# Revit family: IS_ConnectAir_A7012_BIM_DE
name_source: partatom
category: Plumbing Fixtures
revit_build: Autodesk Revit MEP 2015 (Build: 20140606_1530(x64)
units: mm (PartAtom-declared; Revit-internal decimal feet)

## types (1)
- A7012AA - CONNCT AIR BSN MXR RMTD SLM GR PU/M
    BIMobject category = Taps & Mixers
    BOSUseNativeGeometries = 1
    Brand url = www.idealstandard.com
    EAN code = https://4015413341899
    Edition number = 1
    Installation instructions = www.idealstandard.de\produkte
    Manufacturer name = Ideal Standard
    Material main = Brass
    Model = A7012AA
    Nominal height = 0
    Nominal width = 0
    Product Guid = ffff0267-33e0-44f8-a582-1ca4262deac9
    Product SKU = A7012
    Product data url = https://bimobject.com
    Product name = Connect Air Basin Mixer  Slim Gr Pu/M
    Product url = http://www.idealspec.co.uk
    QR code = http://bimobject.com
    Technical description = http://www.idealspec.co.uk
    Uniclass 2015 Code = Pr_40_20_87_98
    Uniclass 2015 Name = Washbasin taps
    Weight Net (Kg) = 0

## geometry (parser evidence)
native form markers: Blend x4, Sweep x1
no freeform markers — native parametric forms only
